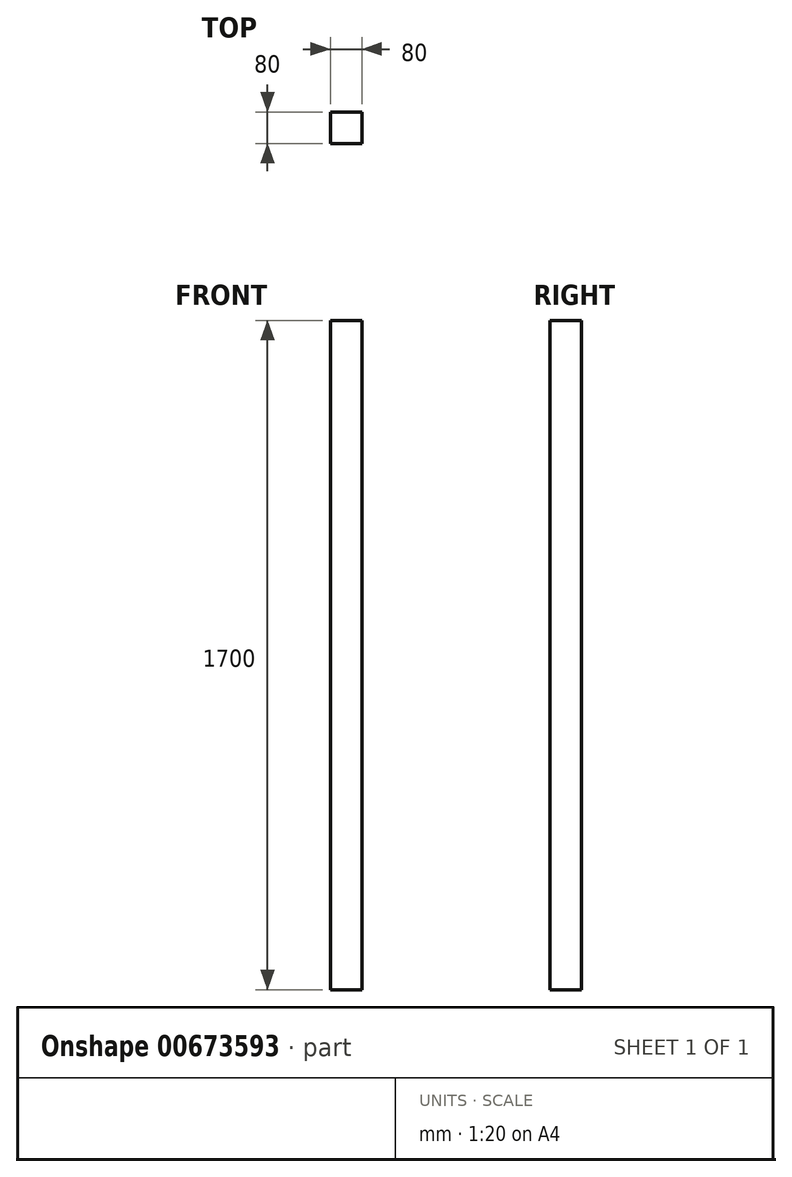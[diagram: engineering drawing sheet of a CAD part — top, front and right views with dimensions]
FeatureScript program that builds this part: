
annotation { "Feature Type Name" : "Feature", "Feature Type Description" : "" }
export const myFeature = defineFeature(function(context is Context, id is Id, definition is map)
    precondition{}
    {
        {
            var Q0;
            Q0=qCreatedBy(makeId("Top.planeOp"),FACE);
            var sketch = newSketch(context, id + "F0", { "sketchPlane" : qUnion([Q0])});
            skLineSegment(sketch, "E0.bottom", {"start": v(40, -40) * mm, "end": v(-40, -40) * mm});
            skLineSegment(sketch, "E0.top", {"start": v(40, 40) * mm, "end": v(-40, 40) * mm});
            skLineSegment(sketch, "E0.left", {"start": v(40, -40) * mm, "end": v(40, 40) * mm});
            skLineSegment(sketch, "E0.right", {"start": v(-40, -40) * mm, "end": v(-40, 40) * mm});
            skPoint(sketch, "E0.middle", {"position": v(0, 0) * mm});
            skSolve(sketch);
        }
        {
            var Q0;
            Q0=makeQuery(id+"F0.imprint","IMPRINT",FACE,{"disambiguationData":[TD([[makeQuery(id+"F0.imprint","IMPRINT",EDGE,{"derivedFrom":sQuery(id+"F0.wireOp",EDGE,"E0.bottom")}),-1.0]])]});
            extrude(context, id + "F1", {"entities" : qUnion([Q0]), "depth" : 1700 * mm, "offsetDistance" : 25 * mm});
        }
    });
